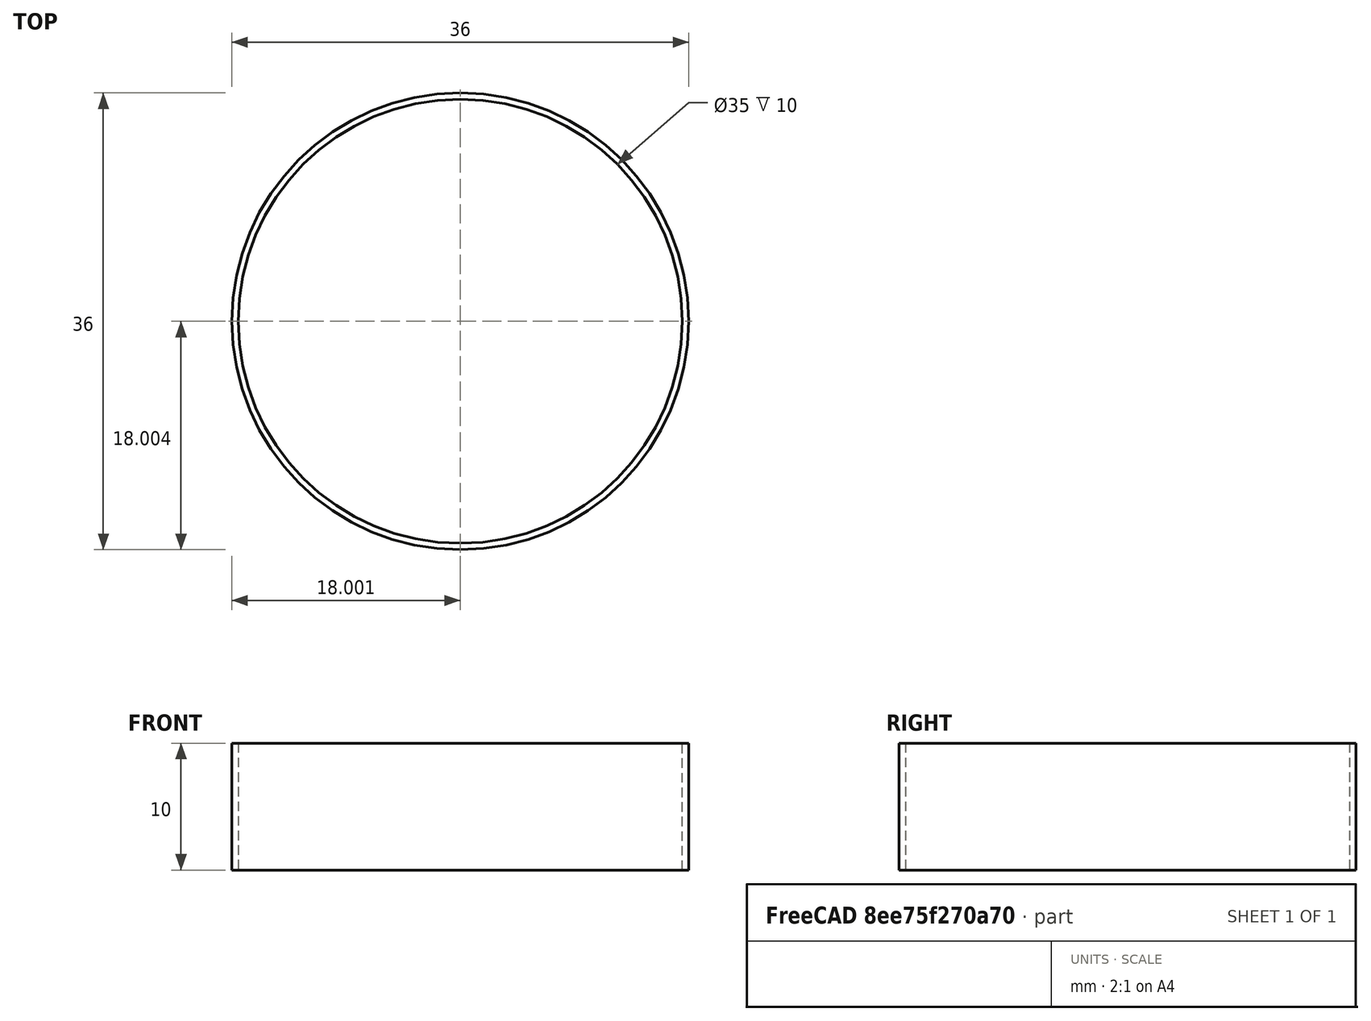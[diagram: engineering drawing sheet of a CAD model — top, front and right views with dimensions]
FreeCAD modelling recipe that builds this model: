
FCSTD DOCUMENT  (FreeCAD 0.20R29603 (Git))
Label: small_pill
License: All rights reserved
LicenseURL: http://en.wikipedia.org/wiki/All_rights_reserved
objects: Sketcher::SketchObject×1, PartDesign::Pad×1, PartDesign::Body×1
note: 4 computed .brp shape members not serialized (recipe doc carries the construction recipe); baked Part::Feature solids carry a one-line shape summary decoded from their .brp

FEATURE [Sketcher::SketchObject] Sketch
  FullyConstrained = true
  MapMode = 5
  Support = -> [XY_Plane]
  sketch-geometry (2):
    g0: Circle CenterX=-3.54942 CenterY=0.594369 CenterZ=0 NormalX=0 NormalY=0 NormalZ=1 AngleXU=0 Radius=18
    g1: Circle CenterX=-3.54942 CenterY=0.594369 CenterZ=0 NormalX=0 NormalY=0 NormalZ=1 AngleXU=0 Radius=17.5
  constraints (4):
    c: Diameter(g0) = 36  'small pill'
    c: Block(g0)
    c: Diameter(g1) = 35
    c: Coincident(g0,g1)
FEATURE [PartDesign::Pad] Pad
  Direction = (0,0,1)
  Length = 10
  Length2 = 10
  Profile = -> Sketch
  ReferenceAxis = -> Sketch [N_Axis]
  Type = 0
FEATURE [PartDesign::Body] Body
  Group = -> [Sketch,Pad]
  Origin = -> Origin
  Tip = -> Pad
